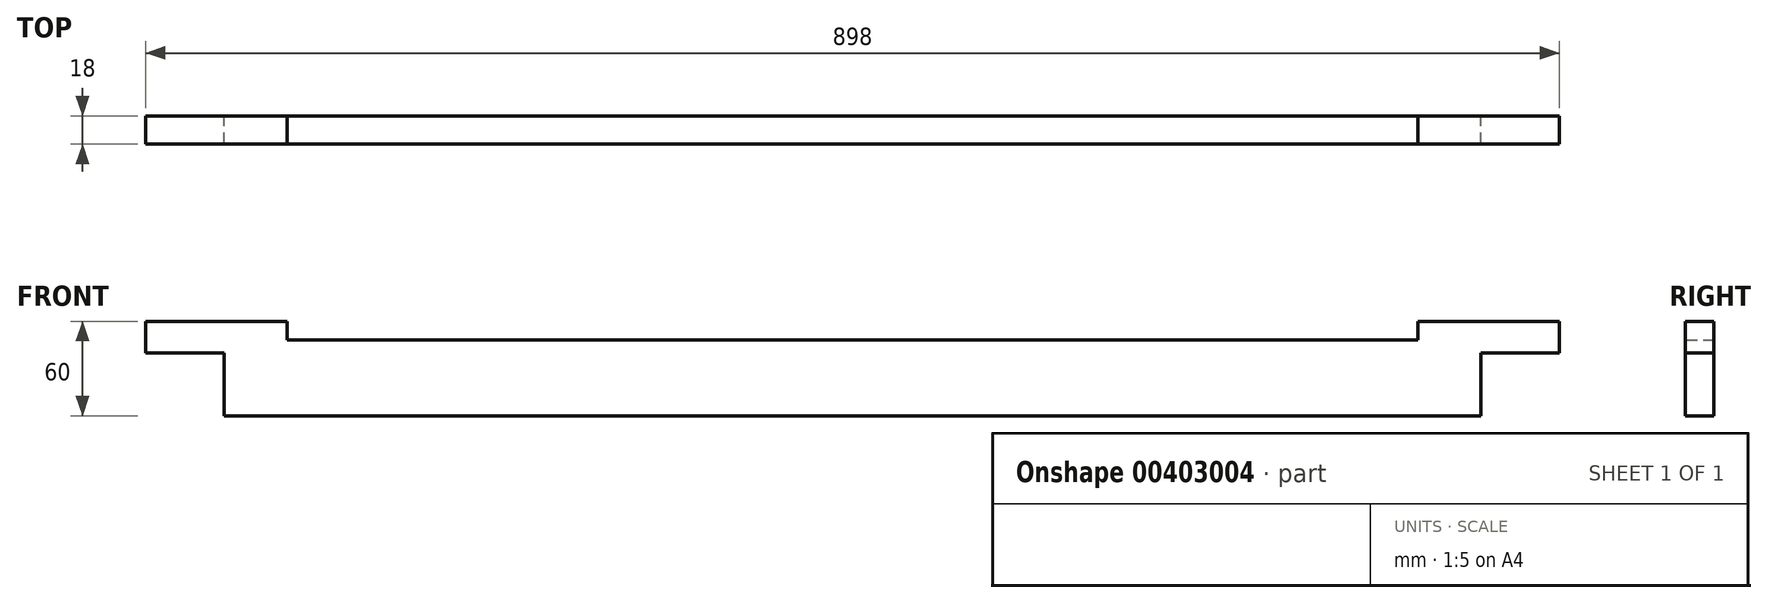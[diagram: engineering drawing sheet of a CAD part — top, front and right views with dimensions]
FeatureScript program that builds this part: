
annotation { "Feature Type Name" : "Feature", "Feature Type Description" : "" }
export const myFeature = defineFeature(function(context is Context, id is Id, definition is map)
    precondition{}
    {
        {
            var Q0;
            Q0=qCreatedBy(makeId("Front.planeOp"),FACE);
            var sketch = newSketch(context, id + "F0", { "sketchPlane" : qUnion([Q0])});
            skLineSegment(sketch, "E0.bottom", {"start": v(0, 0) * mm, "end": v(50, 0) * mm});
            skLineSegment(sketch, "E0.top", {"start": v(0, 20) * mm, "end": v(90, 20) * mm});
            skLineSegment(sketch, "E0.left", {"start": v(0, 0) * mm, "end": v(0, 20) * mm});
            skLineSegment(sketch, "E0.right", {"start": v(898, 0) * mm, "end": v(898, 20) * mm});
            skLineSegment(sketch, "E1.top", {"start": v(50, -40) * mm, "end": v(848, -40) * mm});
            skLineSegment(sketch, "E1.left", {"start": v(50, 0) * mm, "end": v(50, -40) * mm});
            skLineSegment(sketch, "E1.right", {"start": v(848, 0) * mm, "end": v(848, -40) * mm});
            skLineSegment(sketch, "E2.trimOffspring", {"start": v(848, 0) * mm, "end": v(898, 0) * mm});
            skLineSegment(sketch, "E3.top", {"start": v(90, 8) * mm, "end": v(808, 8) * mm});
            skLineSegment(sketch, "E3.left", {"start": v(90, 20) * mm, "end": v(90, 8) * mm});
            skLineSegment(sketch, "E3.right", {"start": v(808, 20) * mm, "end": v(808, 8) * mm});
            skLineSegment(sketch, "E4.trimOffspring", {"start": v(808, 20) * mm, "end": v(898, 20) * mm});
            skSolve(sketch);
        }
        {
            var Q0;
            Q0=makeQuery(id+"F0.imprint","IMPRINT",FACE,{"disambiguationData":[TD([[makeQuery(id+"F0.imprint","IMPRINT",EDGE,{"derivedFrom":sQuery(id+"F0.wireOp",EDGE,"kHmZVxOG-gPJc-REYJ-O9rl-HYASeAGw87Q2.right")}),1.0]])]});
            var Q1;
            Q1=makeQuery(id+"F0.imprint","IMPRINT",FACE,{"disambiguationData":[TD([[makeQuery(id+"F0.imprint","IMPRINT",EDGE,{"derivedFrom":sQuery(id+"F0.wireOp",EDGE,"E0.bottom")}),1.0]])]});
            extrude(context, id + "F1", {"entities" : qUnion([Q0, Q1]), "depth" : 18 * mm});
        }
    });
